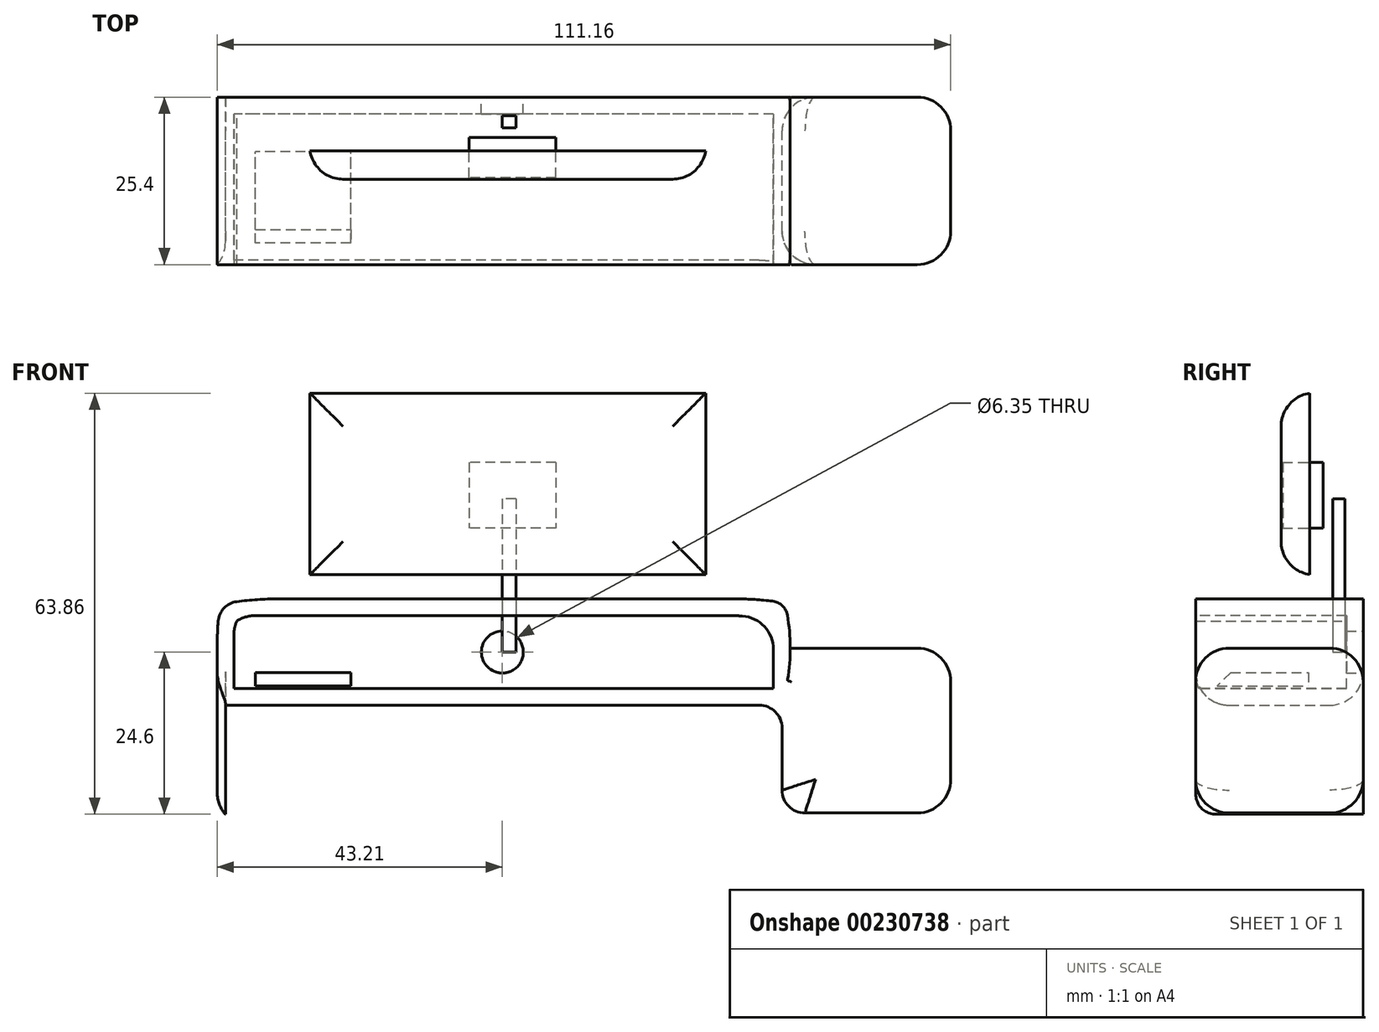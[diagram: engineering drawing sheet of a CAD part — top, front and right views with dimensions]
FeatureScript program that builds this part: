
annotation { "Feature Type Name" : "Feature", "Feature Type Description" : "" }
export const myFeature = defineFeature(function(context is Context, id is Id, definition is map)
    precondition{}
    {
        {
            var Q0;
            Q0=qCreatedBy(makeId("Front.planeOp"),FACE);
            var sketch = newSketch(context, id + "F0", { "sketchPlane" : qUnion([Q0])});
            skLineSegment(sketch, "E0.bottom", {"start": v(42.8, 8.06) * mm, "end": v(-42.8, 8.06) * mm});
            skLineSegment(sketch, "E0.top", {"start": v(42.8, -8.06) * mm, "end": v(-42.8, -8.06) * mm});
            skLineSegment(sketch, "E0.left", {"start": v(42.8, 8.06) * mm, "end": v(42.8, -8.06) * mm});
            skLineSegment(sketch, "E0.right", {"start": v(-42.8, 8.06) * mm, "end": v(-42.8, -8.06) * mm});
            skPoint(sketch, "E0.middle", {"position": v(0, 0) * mm});
            skSolve(sketch);
        }
        {
            var Q0;
            Q0 = qSketchRegion(id + "F0", true);
            extrude(context, id + "F1", {"entities" : qUnion([Q0]), "depth" : 25.4 * mm});
        }
        {
            var Q0;
            Q0=qCreatedBy(makeId("Front.planeOp"),FACE);
            var sketch = newSketch(context, id + "F2", { "sketchPlane" : qUnion([Q0])});
            skLineSegment(sketch, "E1.bottom", {"start": v(-41.97, -24.6) * mm, "end": v(-43.2, -24.6) * mm});
            skLineSegment(sketch, "E1.top", {"start": v(-41.97, 7.24) * mm, "end": v(-43.2, 7.24) * mm});
            skLineSegment(sketch, "E1.left", {"start": v(-41.97, -24.6) * mm, "end": v(-41.97, 7.24) * mm});
            skLineSegment(sketch, "E1.right", {"start": v(-43.2, -24.6) * mm, "end": v(-43.2, 7.24) * mm});
            skPoint(sketch, "E1.middle", {"position": v(-42.59, -8.68) * mm});
            skLineSegment(sketch, "E2.bottom", {"start": v(43.62, -24.4) * mm, "end": v(42.38, -24.4) * mm});
            skLineSegment(sketch, "E2.top", {"start": v(43.62, 7.44) * mm, "end": v(42.38, 7.44) * mm});
            skLineSegment(sketch, "E2.left", {"start": v(43.62, -24.4) * mm, "end": v(43.62, 7.44) * mm});
            skLineSegment(sketch, "E2.right", {"start": v(42.38, -24.4) * mm, "end": v(42.38, 7.44) * mm});
            skPoint(sketch, "E2.middle", {"position": v(43, -8.48) * mm});
            skSolve(sketch);
        }
        {
            var Q0;
            Q0 = qSketchRegion(id + "F2", true);
            extrude(context, id + "F3", {"entities" : qUnion([Q0]), "operationType" : NewBodyOperationType.ADD, "offsetDistance" : 25.4 * mm, "depth" : 25.4 * mm});
        }
        {
            var Q0;
            Q0 = qSketchRegion(id + "F2", true);
            extrude(context, id + "F4", {"entities" : qUnion([Q0]), "operationType" : NewBodyOperationType.ADD, "depth" : 25.4 * mm});
        }
        {
            var Q0;
            Q0 = qSketchRegion(id + "F0", true);
            extrude(context, id + "F5", {"entities" : qUnion([Q0]), "operationType" : NewBodyOperationType.ADD, "depth" : 25.4 * mm});
        }
        {
            var Q0;
            Q0=makeQuery(id+"F3.boolean.opBoolean","MERGE",FACE,{"derivedFrom":[makeQuery(id+"F1.opExtrude","CAP_FACE",FACE,{"disambiguationData":[OSD([sQuery(id+"F0.wireOp",EDGE,"E0.bottom"),sQuery(id+"F0.wireOp",EDGE,"E0.top"),sQuery(id+"F0.wireOp",EDGE,"E0.left"),sQuery(id+"F0.wireOp",EDGE,"E0.right")])],"isStart":false}),makeQuery(id+"F3.opExtrude","CAP_FACE",FACE,{"disambiguationData":[OSD([sQuery(id+"F2.wireOp",EDGE,"E1.bottom"),sQuery(id+"F2.wireOp",EDGE,"E1.top"),sQuery(id+"F2.wireOp",EDGE,"E1.left"),sQuery(id+"F2.wireOp",EDGE,"E1.right")])],"isStart":false}),makeQuery(id+"F3.opExtrude","CAP_FACE",FACE,{"disambiguationData":[OSD([sQuery(id+"F2.wireOp",EDGE,"E2.bottom"),sQuery(id+"F2.wireOp",EDGE,"E2.top"),sQuery(id+"F2.wireOp",EDGE,"E2.left"),sQuery(id+"F2.wireOp",EDGE,"E2.right")])],"isStart":false})]});
            shell(context, id + "F6", {"entities" : qUnion([Q0]), "thickness" : 2.54 * mm});
        }
        {
            var Q0;
            Q0=sQuery(id+"F0.wireOp",VERTEX,"E0.middle");
            var Q1;
            Q1=makeQuery(id+"F1.opExtrude","SWEPT_BODY",BODY,{"disambiguationData":[OSD([sQuery(id+"F0.wireOp",EDGE,"E0.bottom"),sQuery(id+"F0.wireOp",EDGE,"E0.top"),sQuery(id+"F0.wireOp",EDGE,"E0.left"),sQuery(id+"F0.wireOp",EDGE,"E0.right")])]});
            hole(context, id + "F7", {"style" : HoleStyle.SIMPLE, "endStyle" : HoleEndStyle.THROUGH, "oppositeDirection" : true, "holeDiameter" : 6.35 * mm, "locations" : qUnion([Q0]), "scope" : qUnion([Q1]), "isTappedThrough" : true});
        }
        {
            var Q0;
            Q0=makeQuery(id+"F1.opExtrude","SWEPT_EDGE",EDGE,{"disambiguationData":[OSD([sQuery(id+"F0.wireOp",EDGE,"E0.bottom"),sQuery(id+"F0.wireOp",EDGE,"E0.right")])]});
            var Q1;
            Q1=makeQuery(id+"F3.opExtrude","SWEPT_EDGE",EDGE,{"disambiguationData":[OSD([sQuery(id+"F2.wireOp",EDGE,"E1.top"),sQuery(id+"F2.wireOp",EDGE,"E1.right")])]});
            fillet(context, id + "F8", {"entities" : qUnion([Q0, Q1]), "radius" : 47.22 * mm, "tangentPropagation" : true, "allowEdgeOverflow" : false});
        }
        {
            var Q0;
            Q0=makeQuery(id+"F3.opExtrude","SWEPT_EDGE",EDGE,{"disambiguationData":[OSD([sQuery(id+"F2.wireOp",EDGE,"E2.top"),sQuery(id+"F2.wireOp",EDGE,"E2.left")])]});
            fillet(context, id + "F9", {"entities" : qUnion([Q0]), "radius" : 28.82 * mm, "tangentPropagation" : true, "allowEdgeOverflow" : false});
        }
        {
            var Q0;
            Q0=makeQuery(id+"F1.opExtrude","SWEPT_EDGE",EDGE,{"disambiguationData":[OSD([sQuery(id+"F0.wireOp",EDGE,"E0.bottom"),sQuery(id+"F0.wireOp",EDGE,"E0.left")])]});
            fillet(context, id + "F10", {"entities" : qUnion([Q0]), "radius" : 42.31 * mm, "tangentPropagation" : true, "allowEdgeOverflow" : false});
        }
        {
            var Q0;
            Q0=makeQuery(id+"F10.opFillet","BLEND_EDGE",EDGE,{"blendedFrom":[makeQuery(id+"F1.opExtrude","SWEPT_EDGE",EDGE,{"disambiguationData":[OSD([sQuery(id+"F0.wireOp",EDGE,"E0.bottom"),sQuery(id+"F0.wireOp",EDGE,"E0.left")])]}),makeQuery(id+"F9.opFillet","BLEND_FACE",FACE,{"disambiguationData":[OSD([sQuery(id+"F2.wireOp",EDGE,"E2.top"),sQuery(id+"F2.wireOp",EDGE,"E2.left")])]})],"blendedInto":[makeQuery(id+"F9.opFillet","BLEND_FACE",FACE,{"disambiguationData":[OSD([sQuery(id+"F2.wireOp",EDGE,"E2.top"),sQuery(id+"F2.wireOp",EDGE,"E2.left")])]})]});
            fillet(context, id + "F11", {"entities" : qUnion([Q0]), "radius" : 2.6 * mm, "tangentPropagation" : true, "allowEdgeOverflow" : false});
        }
        {
            var Q0;
            Q0=makeQuery(id+"F8.opFillet","BLEND_EDGE",EDGE,{"blendedFrom":[makeQuery(id+"F1.opExtrude","SWEPT_EDGE",EDGE,{"disambiguationData":[OSD([sQuery(id+"F0.wireOp",EDGE,"E0.bottom"),sQuery(id+"F0.wireOp",EDGE,"E0.right")])]}),makeQuery(id+"F3.opExtrude","SWEPT_EDGE",EDGE,{"disambiguationData":[OSD([sQuery(id+"F2.wireOp",EDGE,"E1.top"),sQuery(id+"F2.wireOp",EDGE,"E1.right")])]})],"blendedInto":[]});
            fillet(context, id + "F12", {"entities" : qUnion([Q0]), "radius" : 3.26 * mm, "tangentPropagation" : true, "allowEdgeOverflow" : false});
        }
        {
            var Q0;
            Q0=qCreatedBy(makeId("Front.planeOp"),FACE);
            var sketch = newSketch(context, id + "F13", { "sketchPlane" : qUnion([Q0])});
            skLineSegment(sketch, "E3.bottom", {"start": v(-22.95, -3.1) * mm, "end": v(-37.42, -3.1) * mm});
            skLineSegment(sketch, "E3.top", {"start": v(-22.95, -5.17) * mm, "end": v(-37.42, -5.17) * mm});
            skLineSegment(sketch, "E3.left", {"start": v(-22.95, -3.1) * mm, "end": v(-22.95, -5.17) * mm});
            skLineSegment(sketch, "E3.right", {"start": v(-37.42, -3.1) * mm, "end": v(-37.42, -5.17) * mm});
            skPoint(sketch, "E3.middle", {"position": v(-30.18, -4.13) * mm});
            skSolve(sketch);
        }
        {
            var Q0;
            Q0 = qSketchRegion(id + "F13", true);
            extrude(context, id + "F14", {"entities" : qUnion([Q0]), "depth" : 22.6 * mm, "hasSecondDirection" : true, "secondDirectionOppositeDirection" : false, "secondDirectionDepth" : 8.3 * mm});
        }
        {
            var Q0;
            Q0=makeQuery(id+"F14.opExtrude","CAP_EDGE",EDGE,{"disambiguationData":[OSD([sQuery(id+"F13.wireOp",EDGE,"E3.bottom")])],"isStart":false});
            chamfer(context, id + "F15", {"entities" : qUnion([Q0]), "width" : 2.54 * mm, "tangentPropagation" : true});
        }
        {
            var Q0;
            Q0=qCreatedBy(makeId("Front.planeOp"),FACE);
            var sketch = newSketch(context, id + "F16", { "sketchPlane" : qUnion([Q0])});
            skLineSegment(sketch, "E4.bottom", {"start": v(-29.16, 39.26) * mm, "end": v(30.82, 39.26) * mm});
            skLineSegment(sketch, "E4.top", {"start": v(-29.16, 11.75) * mm, "end": v(30.82, 11.75) * mm});
            skLineSegment(sketch, "E4.left", {"start": v(-29.16, 39.26) * mm, "end": v(-29.16, 11.75) * mm});
            skLineSegment(sketch, "E4.right", {"start": v(30.82, 39.26) * mm, "end": v(30.82, 11.75) * mm});
            skSolve(sketch);
        }
        {
            var Q0;
            Q0 = qSketchRegion(id + "F16", true);
            extrude(context, id + "F17", {"entities" : qUnion([Q0]), "depth" : 12.45 * mm, "hasSecondDirection" : true, "secondDirectionOppositeDirection" : false, "secondDirectionDepth" : 8.13 * mm});
        }
        {
            var Q0;
            Q0=qCreatedBy(makeId("Front.planeOp"),FACE);
            var sketch = newSketch(context, id + "F18", { "sketchPlane" : qUnion([Q0])});
            skLineSegment(sketch, "E5.bottom", {"start": v(8.12, 28.74) * mm, "end": v(-5.02, 28.74) * mm});
            skLineSegment(sketch, "E5.top", {"start": v(8.12, 18.78) * mm, "end": v(-5.02, 18.78) * mm});
            skLineSegment(sketch, "E5.left", {"start": v(8.12, 28.74) * mm, "end": v(8.12, 18.78) * mm});
            skLineSegment(sketch, "E5.right", {"start": v(-5.02, 28.74) * mm, "end": v(-5.02, 18.78) * mm});
            skSolve(sketch);
        }
        {
            var Q0;
            Q0 = qSketchRegion(id + "F18", true);
            extrude(context, id + "F19", {"entities" : qUnion([Q0]), "depth" : 12.2 * mm, "hasSecondDirection" : true, "secondDirectionOppositeDirection" : false, "secondDirectionDepth" : 6.1 * mm});
        }
        {
            var Q0;
            Q0=qCreatedBy(makeId("Front.planeOp"),FACE);
            var sketch = newSketch(context, id + "F20", { "sketchPlane" : qUnion([Q0])});
            skLineSegment(sketch, "E6", {"start": v(3.88, 24.62) * mm, "end": v(18.93, 7.3) * mm});
            skSolve(sketch);
        }
        {
            var Q0;
            Q0=qCreatedBy(makeId("Front.planeOp"),FACE);
            var sketch = newSketch(context, id + "F21", { "sketchPlane" : qUnion([Q0])});
            skFitSpline(sketch, "E7", {"points": [v(-22.66, -4.23) * mm, v(0, 0) * mm, v(-23.06, -5.14) * mm, v(-23.32, -4.45) * mm, v(-22.66, -4.23) * mm]});
            skSolve(sketch);
        }
        {
            var Q0;
            Q0=sQuery(id+"F20.wireOp",EDGE,"E6");
            extrude(context, id + "F22", {"bodyType" : ToolBodyType.SURFACE, "surfaceEntities" : qUnion([Q0]), "depth" : 5.84 * mm, "hasSecondDirection" : true, "secondDirectionOppositeDirection" : false, "secondDirectionDepth" : 3.56 * mm});
        }
        {
            var Q0;
            Q0=sQuery(id+"F21.wireOp",EDGE,"E7");
            extrude(context, id + "F23", {"bodyType" : ToolBodyType.SURFACE, "surfaceEntities" : qUnion([Q0]), "depth" : 7.87 * mm, "hasSecondDirection" : true, "secondDirectionOppositeDirection" : false, "secondDirectionDepth" : 6.98 * mm});
        }
        {
            var Q0;
            Q0=qCreatedBy(makeId("Front.planeOp"),FACE);
            var sketch = newSketch(context, id + "F24", { "sketchPlane" : qUnion([Q0])});
            skLineSegment(sketch, "E8.bottom", {"start": v(2.05, 23.21) * mm, "end": v(0, 23.21) * mm});
            skLineSegment(sketch, "E8.top", {"start": v(2.05, 0) * mm, "end": v(0, 0) * mm});
            skLineSegment(sketch, "E8.left", {"start": v(2.05, 23.21) * mm, "end": v(2.05, 0) * mm});
            skLineSegment(sketch, "E8.right", {"start": v(0, 23.21) * mm, "end": v(0, 0) * mm});
            skSolve(sketch);
        }
        {
            var Q0;
            Q0 = qSketchRegion(id + "F24", true);
            extrude(context, id + "F25", {"entities" : qUnion([Q0]), "depth" : 4.64 * mm, "hasSecondDirection" : true, "secondDirectionOppositeDirection" : false, "secondDirectionDepth" : 2.8 * mm});
        }
        {
            var Q0;
            Q0=makeQuery(id+"F3.opExtrude","SWEPT_FACE",FACE,{"disambiguationData":[OSD([sQuery(id+"F2.wireOp",EDGE,"E2.left")])]});
            extrude(context, id + "F26", {"entities" : qUnion([Q0]), "operationType" : NewBodyOperationType.ADD, "depth" : 24.32 * mm});
        }
        {
            var Q0;
            Q0=makeQuery(id+"F3.opExtrude","SWEPT_EDGE",EDGE,{"disambiguationData":[OSD([sQuery(id+"F2.wireOp",EDGE,"E2.bottom"),sQuery(id+"F2.wireOp",EDGE,"E2.right")])]});
            var Q1;
            Q1=makeQuery(id+"F3.boolean.opBoolean","INTERSECT",EDGE,{"derivedFrom":[makeQuery(id+"F1.opExtrude","SWEPT_FACE",FACE,{"disambiguationData":[OSD([sQuery(id+"F0.wireOp",EDGE,"E0.top")])]}),makeQuery(id+"F3.opExtrude","SWEPT_FACE",FACE,{"disambiguationData":[OSD([sQuery(id+"F2.wireOp",EDGE,"E2.right")])]})]});
            fillet(context, id + "F27", {"entities" : qUnion([Q0, Q1]), "radius" : 3.46 * mm, "tangentPropagation" : true, "allowEdgeOverflow" : false});
        }
        {
            var Q0;
            Q0=makeQuery(id+"F6.opShell","OFFSET_EDGE",EDGE,{"disambiguationData":[OSD([sQuery(id+"F2.wireOp",EDGE,"E2.top"),sQuery(id+"F2.wireOp",EDGE,"E2.left")])]});
            fillet(context, id + "F28", {"entities" : qUnion([Q0]), "radius" : 12.9 * mm, "tangentPropagation" : true, "allowEdgeOverflow" : false});
        }
        {
            var Q0;
            Q0=makeQuery(id+"F6.opShell","OFFSET_EDGE",EDGE,{"disambiguationData":[OSD([sQuery(id+"F0.wireOp",EDGE,"E0.bottom"),sQuery(id+"F0.wireOp",EDGE,"E0.left")])]});
            fillet(context, id + "F29", {"entities" : qUnion([Q0]), "radius" : 26.56 * mm, "tangentPropagation" : true, "allowEdgeOverflow" : false});
        }
        {
            var Q0;
            Q0=makeQuery(id+"F29.opFillet","BLEND_EDGE",EDGE,{"blendedFrom":[makeQuery(id+"F6.opShell","OFFSET_EDGE",EDGE,{"disambiguationData":[OSD([sQuery(id+"F0.wireOp",EDGE,"E0.bottom"),sQuery(id+"F0.wireOp",EDGE,"E0.left")])]}),makeQuery(id+"F28.opFillet","BLEND_FACE",FACE,{"disambiguationData":[OSD([sQuery(id+"F2.wireOp",EDGE,"E2.top"),sQuery(id+"F2.wireOp",EDGE,"E2.left")])]})],"blendedInto":[makeQuery(id+"F28.opFillet","BLEND_FACE",FACE,{"disambiguationData":[OSD([sQuery(id+"F2.wireOp",EDGE,"E2.top"),sQuery(id+"F2.wireOp",EDGE,"E2.left")])]})]});
            fillet(context, id + "F30", {"entities" : qUnion([Q0]), "radius" : 5.08 * mm, "tangentPropagation" : true, "allowEdgeOverflow" : false});
        }
        {
            var Q0;
            Q0=makeQuery(id+"F17.opExtrude","CAP_FACE",FACE,{"disambiguationData":[OSD([sQuery(id+"F16.wireOp",EDGE,"E4.bottom"),sQuery(id+"F16.wireOp",EDGE,"E4.top"),sQuery(id+"F16.wireOp",EDGE,"E4.left"),sQuery(id+"F16.wireOp",EDGE,"E4.right")])],"isStart":false});
            fillet(context, id + "F31", {"entities" : qUnion([Q0]), "radius" : 5.08 * mm, "tangentPropagation" : true, "allowEdgeOverflow" : false});
        }
        {
            var Q0;
            Q0=makeQuery(id+"F26.opExtrude","CAP_EDGE",EDGE,{"disambiguationData":[OSD([sQuery(id+"F2.wireOp",EDGE,"E2.bottom"),sQuery(id+"F2.wireOp",EDGE,"E2.left")])],"isStart":false});
            fillet(context, id + "F32", {"entities" : qUnion([Q0]), "radius" : 5.08 * mm, "tangentPropagation" : true, "allowEdgeOverflow" : false});
        }
        {
            var Q0;
            Q0=makeQuery(id+"F26.opExtrude","CAP_EDGE",EDGE,{"disambiguationData":[OSD([sQuery(id+"F2.wireOp",EDGE,"E2.top"),sQuery(id+"F2.wireOp",EDGE,"E2.left")])],"isStart":false});
            fillet(context, id + "F33", {"entities" : qUnion([Q0]), "radius" : 5.08 * mm, "tangentPropagation" : true, "allowEdgeOverflow" : false});
        }
        {
            var Q0;
            Q0=makeQuery(id+"F26.opExtrude","CAP_FACE",FACE,{"disambiguationData":[OSD([sQuery(id+"F2.wireOp",EDGE,"E2.left")])],"isStart":false});
            fillet(context, id + "F34", {"entities" : qUnion([Q0]), "radius" : 5.08 * mm, "tangentPropagation" : true, "allowEdgeOverflow" : false});
        }
        {
            var Q0;
            Q0=makeQuery(id+"F6.opShell","OFFSET_EDGE",EDGE,{"disambiguationData":[OSD([sQuery(id+"F0.wireOp",EDGE,"E0.bottom"),sQuery(id+"F0.wireOp",EDGE,"E0.right")])]});
            var Q1;
            Q1=makeQuery(id+"F6.opShell","OFFSET_EDGE",EDGE,{"disambiguationData":[OSD([sQuery(id+"F2.wireOp",EDGE,"E1.top"),sQuery(id+"F2.wireOp",EDGE,"E1.right")])]});
            fillet(context, id + "F35", {"entities" : qUnion([Q0, Q1]), "radius" : 5.08 * mm, "tangentPropagation" : true, "allowEdgeOverflow" : false});
        }
        {
            var Q0;
            Q0=makeQuery(id+"F3.opExtrude","CAP_EDGE",EDGE,{"disambiguationData":[OSD([sQuery(id+"F2.wireOp",EDGE,"E1.left")])],"isStart":false});
            fillet(context, id + "F36", {"entities" : qUnion([Q0]), "radius" : 5.08 * mm, "tangentPropagation" : true, "allowEdgeOverflow" : false});
        }
        {
            var Q0;
            Q0=makeQuery(id+"F3.opExtrude","SWEPT_EDGE",EDGE,{"disambiguationData":[OSD([sQuery(id+"F2.wireOp",EDGE,"E1.bottom"),sQuery(id+"F2.wireOp",EDGE,"E1.right")])]});
            fillet(context, id + "F37", {"entities" : qUnion([Q0]), "radius" : 5.08 * mm, "tangentPropagation" : true, "allowEdgeOverflow" : false});
        }
        {
            var Q0;
            Q0=sQuery(id+"F0.wireOp",EDGE,"E0.bottom");
            var Q1;
            Q1=sQuery(id+"F2.wireOp",EDGE,"E2.left");
            var Q2;
            Q2=sQuery(id+"F2.wireOp",EDGE,"E1.right");
            var Q3;
            Q3=sQuery(id+"F0.wireOp",EDGE,"E0.top");
            extrude(context, id + "F38", {"bodyType" : ToolBodyType.SURFACE, "surfaceEntities" : qUnion([Q0, Q1, Q2, Q3]), "depth" : 18.74 * mm});
        }
    });
